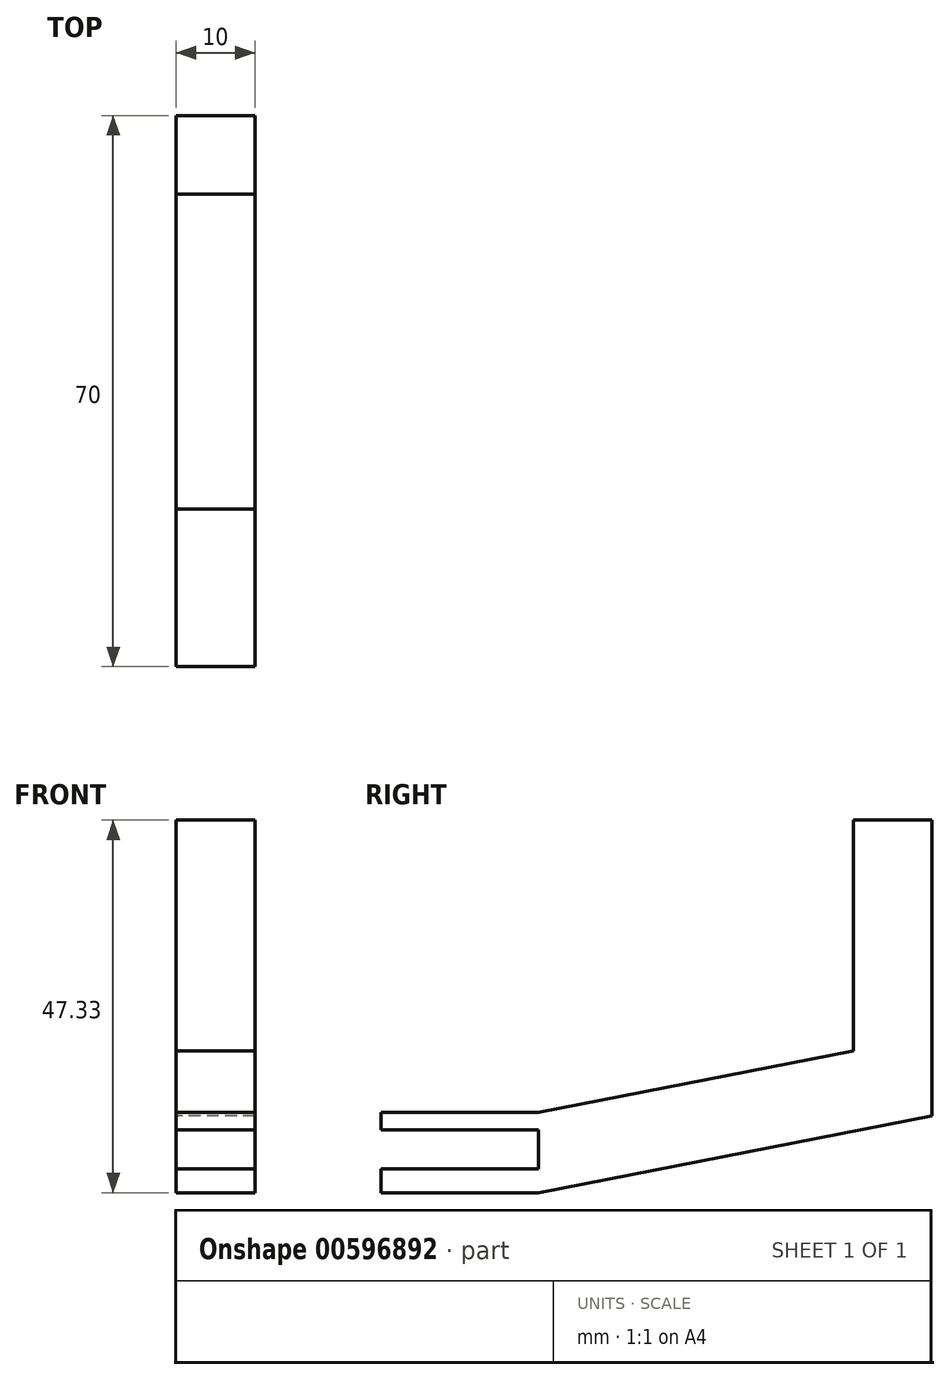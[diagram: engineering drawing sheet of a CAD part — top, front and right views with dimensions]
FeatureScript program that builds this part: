
annotation { "Feature Type Name" : "Feature", "Feature Type Description" : "" }
export const myFeature = defineFeature(function(context is Context, id is Id, definition is map)
    precondition{}
    {
        {
            var Q0;
            Q0=qCreatedBy(makeId("Right.planeOp"),FACE);
            var sketch = newSketch(context, id + "F0", { "sketchPlane" : qUnion([Q0])});
            skLineSegment(sketch, "E0", {"start": v(0, 0) * mm, "end": v(20, 0) * mm});
            skLineSegment(sketch, "E1", {"start": v(20, 0) * mm, "end": v(20, -5) * mm});
            skLineSegment(sketch, "E2", {"start": v(20, -5) * mm, "end": v(0, -5) * mm});
            skLineSegment(sketch, "E3", {"start": v(0, -5) * mm, "end": v(0, -8) * mm});
            skLineSegment(sketch, "E4", {"start": v(0, -8) * mm, "end": v(20, -8) * mm});
            skLineSegment(sketch, "E5", {"start": v(20, -8) * mm, "end": v(70, 1.76) * mm});
            skLineSegment(sketch, "E6", {"start": v(70, 1.76) * mm, "end": v(70, 39.33) * mm});
            skLineSegment(sketch, "E7", {"start": v(70, 39.33) * mm, "end": v(60, 39.33) * mm});
            skLineSegment(sketch, "E8", {"start": v(60, 39.33) * mm, "end": v(60, 10) * mm});
            skLineSegment(sketch, "E9", {"start": v(60, 10) * mm, "end": v(20, 2.19) * mm});
            skLineSegment(sketch, "E10", {"start": v(20, 2.19) * mm, "end": v(0, 2.19) * mm});
            skLineSegment(sketch, "E11", {"start": v(0, 2.19) * mm, "end": v(0, 0) * mm});
            skLineSegment(sketch, "E12", {"start": v(20, -8) * mm, "end": v(85.79, -8) * mm, "construction": true});
            skLineSegment(sketch, "E13", {"start": v(20, -2.5) * mm, "end": v(-45.81, -2.5) * mm, "construction": true});
            skSolve(sketch);
        }
        {
            var Q0;
            Q0 = qSketchRegion(id + "F0", true);
            extrude(context, id + "F1", {"entities" : qUnion([Q0]), "endBound" : BoundingType.SYMMETRIC, "depth" : 10 * mm, "offsetDistance" : 25 * mm});
        }
    });
